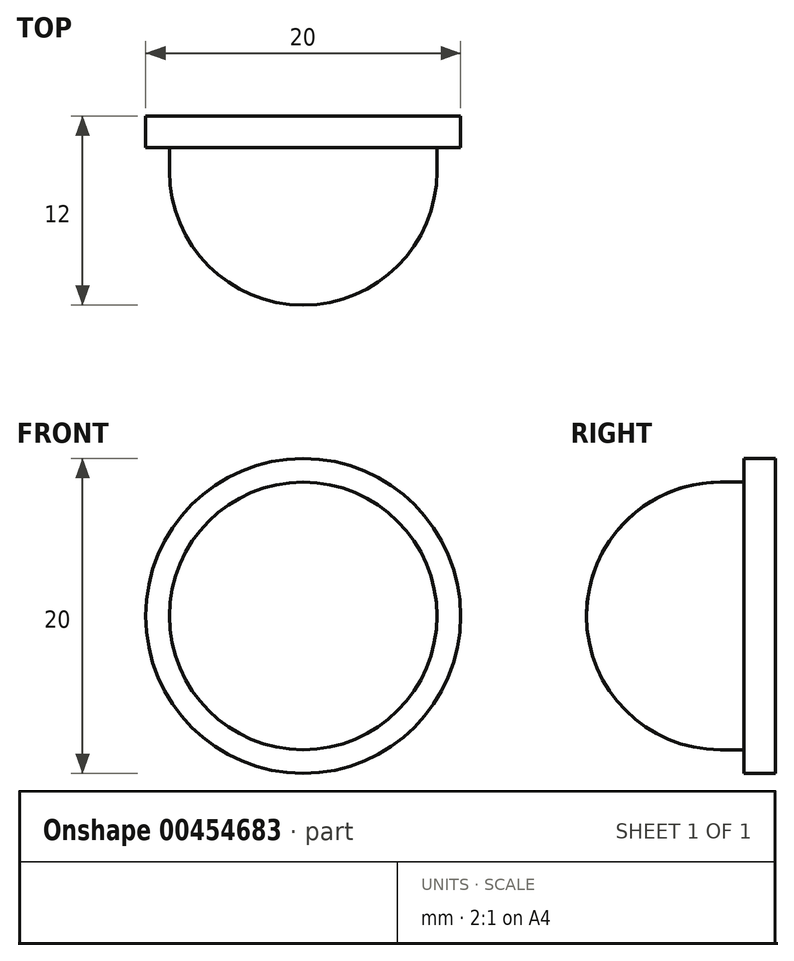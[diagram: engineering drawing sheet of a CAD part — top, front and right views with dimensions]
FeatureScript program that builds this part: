
annotation { "Feature Type Name" : "Feature", "Feature Type Description" : "" }
export const myFeature = defineFeature(function(context is Context, id is Id, definition is map)
    precondition{}
    {
        {
            var Q0;
            Q0=qCreatedBy(makeId("Right.planeOp"),FACE);
            var sketch = newSketch(context, id + "F0", { "sketchPlane" : qUnion([Q0])});
            skLineSegment(sketch, "E0", {"start": v(0, 0) * mm, "end": v(0, 10) * mm});
            skLineSegment(sketch, "E1", {"start": v(0, 10) * mm, "end": v(-2, 10) * mm});
            skLineSegment(sketch, "E2", {"start": v(-2, 10) * mm, "end": v(-2, 8.5) * mm});
            skLineSegment(sketch, "E3", {"start": v(-2, 8.5) * mm, "end": v(-3.5, 8.5) * mm});
            skLineSegment(sketch, "E4", {"start": v(0, 0) * mm, "end": v(-12, 0) * mm});
            skArc(sketch, "E5", {"start": v(-3.5, 8.5) * mm, "mid": v(-9.51, 6.01) * mm, "end": v(-12, 0) * mm});
            skSolve(sketch);
        }
        {
            var Q0;
            Q0=qCreatedBy(makeId("Right.planeOp"),FACE);
            var sketch = newSketch(context, id + "F1", { "sketchPlane" : qUnion([Q0])});
            skLineSegment(sketch, "E6", {"start": v(-24.81, 0) * mm, "end": v(9.37, 0) * mm, "construction": true});
            skSolve(sketch);
        }
        {
            var Q0;
            Q0 = qSketchRegion(id + "F0", true);
            var Q1;
            Q1=sQuery(id+"F1.wireOp",EDGE,"E6");
            revolve(context, id + "F2", {"entities" : qUnion([Q0]), "axis" : qUnion([Q1]), "revolveType" : RevolveType.FULL});
        }
    });
